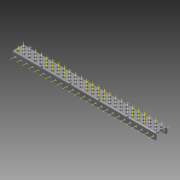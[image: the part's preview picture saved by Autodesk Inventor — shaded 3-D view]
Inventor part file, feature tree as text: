
AUTODESK INVENTOR PART (.ipt)
format: ipt  version: 2015 (Build 190159000, 159)  size: 2,141,696 bytes
history: native  units: in
note: dims shown in document units (in); Inventor stores cm internally (conversion verified against a paired STEP export)
features: other x131, pattern_linear x3, sheet_metal_op x1, extrude x1, imported_body x1, sketch x1
ambient origin geometry x8: Origin, YZ Plane, XZ Plane, XY Plane, X Axis, Y Axis, Z Axis, Center Point
bodies: Body1 (feature_tree)
feature tree (138):
  sheet_metal_op  "Fold1"
  other  "C-Channel"
  extrude  "length cut"  Depth=0.5in
  other  "top axis"
  other  "inner axis"
  other  "front axis"
  other  "back axis"
  pattern_linear  "top axes"  Spacing1=0.5in  [1 undecoded]
  pattern_linear  "inner axes"  Spacing1=0.5in  [1 undecoded]
  pattern_linear  "horiz axes"  Spacing1=-12.5in  [1 undecoded]
  other  "right plane"
  imported_body  "Base1"
  sketch  "Sketch1"  dims[d1=0.0in d4=0.5in d5=0.7874in d7=0.5in d10=0.5in d13=0.5in d14=-12.5in d15=0.0in d16=0.0in d17=0.0in d18=0.0in d19=0.0in]
  other  "Work Point1"
  other  "Work Point2"
  other  "Work Point3"
  other  "Work Point4"
  other  "Work Axis5"
  other  "Work Axis6"
  other  "Work Axis7"
  other  "Work Axis8"
  other  "Work Axis11"
  other  "Work Axis12"
  other  "Work Axis13"
  other  "Work Axis14"
  other  "Work Axis15"
  other  "Work Axis18"
  other  "Work Axis19"
  other  "Work Axis20"
  other  "Work Axis23"
  other  "Work Axis24"
  other  "Work Axis25"
  other  "Work Axis26"
  other  "Work Axis30"
  other  "Work Axis31"
  other  "Work Axis32"
  other  "Work Axis33"
  other  "left plane"
  other  "Work Axis37"
  other  "Work Axis38"
  other  "Work Axis39"
  other  "Work Axis40"
  other  "Work Axis41"
  other  "Work Axis42"
  other  "Work Axis43"
  other  "Work Axis44"
  other  "Work Axis45"
  other  "Work Axis46"
  other  "Work Axis47"
  other  "Work Axis48"
  other  "Work Axis49"
  other  "Work Axis50"
  other  "Work Axis51"
  other  "Work Axis52"
  other  "Work Axis53"
  other  "Work Axis54"
  other  "Work Axis55"
  other  "Work Axis56"
  other  "Work Axis57"
  other  "Work Axis58"
  other  "Work Axis59"
  other  "Work Axis60"
  other  "Work Axis61"
  other  "Work Axis62"
  other  "Work Axis63"
  other  "Work Axis64"
  other  "Work Axis65"
  other  "Work Axis66"
  other  "Work Axis67"
  other  "Work Axis68"
  other  "Work Axis69"
  other  "Work Axis70"
  other  "Work Axis71"
  other  "Work Axis72"
  other  "Work Axis73"
  other  "Work Axis74"
  other  "Work Axis75"
  other  "Work Axis76"
  other  "Work Axis77"
  other  "Work Axis78"
  other  "Work Axis79"
  other  "Work Axis80"
  other  "Work Axis81"
  other  "Work Axis82"
  other  "Work Axis83"
  other  "Work Axis84"
  other  "Work Axis85"
  other  "Work Axis86"
  other  "Work Axis87"
  other  "Work Axis88"
  other  "Work Axis89"
  other  "Work Axis90"
  other  "Work Axis91"
  other  "Work Axis92"
  other  "Work Axis93"
  other  "Work Axis94"
  other  "Work Axis95"
  other  "Work Axis96"
  other  "Work Axis97"
  other  "Work Axis98"
  other  "Work Axis99"
  other  "Work Axis100"
  other  "Work Axis101"
  other  "Work Axis102"
  other  "Work Axis103"
  other  "Work Axis104"
  other  "Work Axis105"
  other  "Work Axis106"
  other  "Work Axis107"
  other  "Work Axis108"
  other  "Work Axis109"
  other  "Work Axis110"
  other  "Work Axis111"
  other  "Work Axis112"
  other  "Work Axis113"
  other  "Work Axis114"
  other  "Work Axis115"
  other  "Work Axis116"
  other  "Work Axis117"
  other  "Work Axis118"
  other  "Work Axis119"
  other  "Work Axis120"
  other  "Work Axis121"
  other  "Work Axis122"
  other  "Work Axis123"
  other  "Work Axis124"
  other  "Work Axis125"
  other  "Work Axis126"
  other  "Work Axis127"
  other  "Work Axis128"
  other  "Work Axis129"
  other  "Work Axis130"
  other  "Work Axis131"
  other  "Work Axis132"
  other  "Work Axis133"
  other  "Work Axis134"
  other  "Work Axis135"
  other  "Work Axis136"
note: 3 required parameter values undecoded (feature->parameter linkage not recoverable at this tier; creation-order binding heuristic only, values carry confidence <= 0.55)
